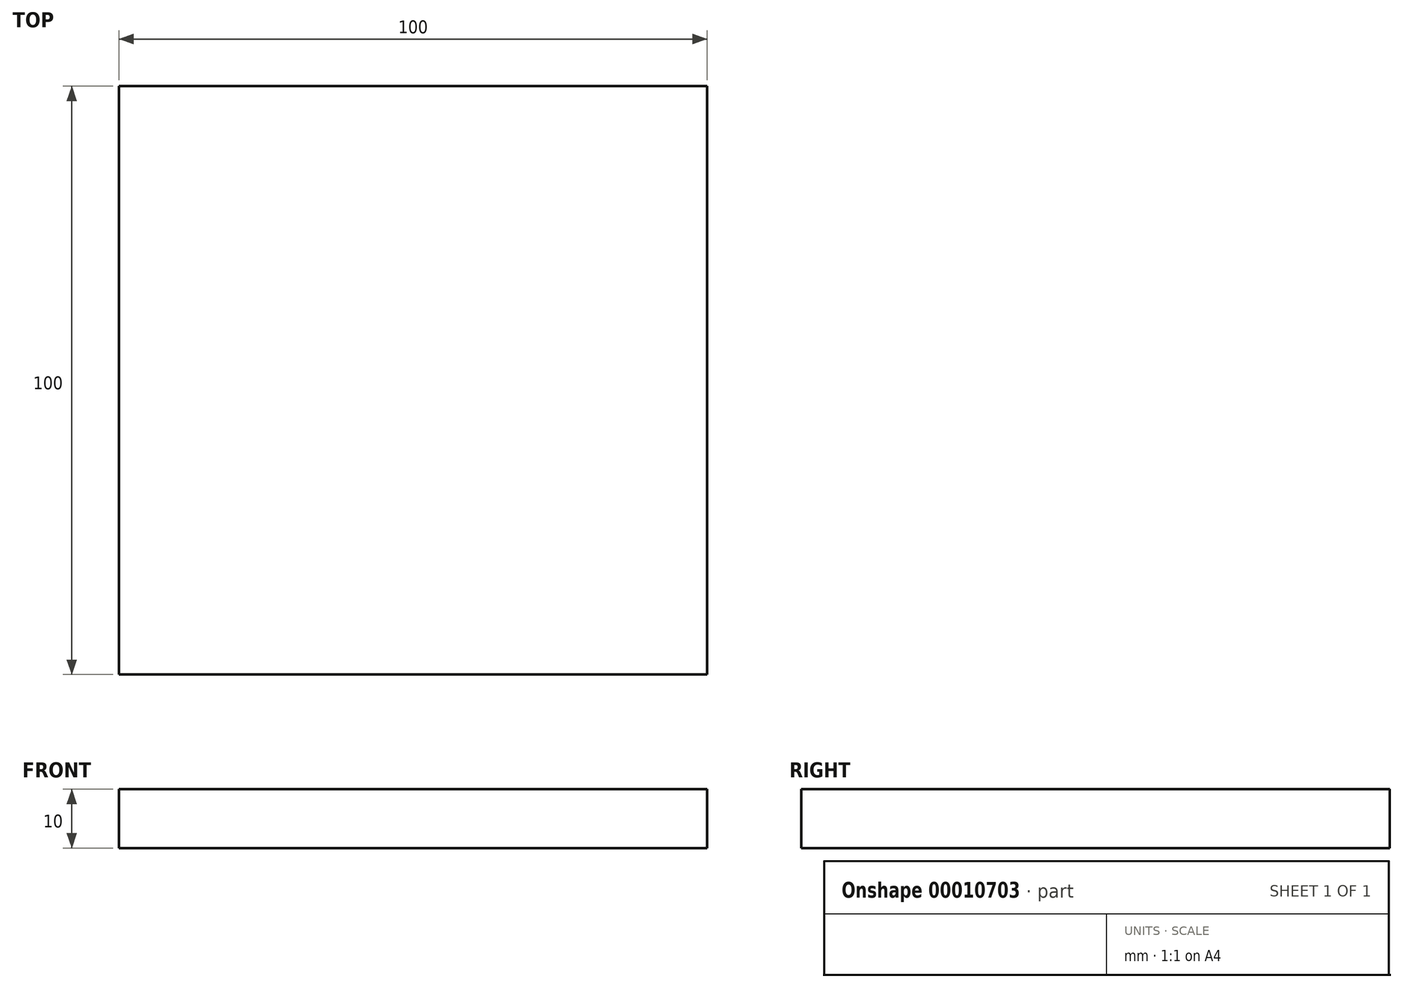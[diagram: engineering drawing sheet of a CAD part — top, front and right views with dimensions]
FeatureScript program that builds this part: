
annotation { "Feature Type Name" : "Feature", "Feature Type Description" : "" }
export const myFeature = defineFeature(function(context is Context, id is Id, definition is map)
    precondition{}
    {
        {
            var Q0;
            Q0=qCreatedBy(makeId("Top.planeOp"),FACE);
            var sketch = newSketch(context, id + "F1", { "sketchPlane" : qUnion([Q0])});
            skLineSegment(sketch, "E0.rect.bottom", {"start": v(50, 50) * mm, "end": v(-50, 50) * mm});
            skLineSegment(sketch, "E0.rect.top", {"start": v(50, -50) * mm, "end": v(-50, -50) * mm});
            skLineSegment(sketch, "E0.rect.left", {"start": v(50, 50) * mm, "end": v(50, -50) * mm});
            skLineSegment(sketch, "E0.rect.right", {"start": v(-50, 50) * mm, "end": v(-50, -50) * mm});
            skPoint(sketch, "E0.rect.middle", {"position": v(0, 0) * mm});
            skPoint(sketch, "E1.rect.bottom.start.orphan", {"position": v(50.55, 50.55) * mm});
            skPoint(sketch, "E1.rect.right.start.orphan", {"position": v(-50.55, 50.55) * mm});
            skPoint(sketch, "E1.rect.top.end.orphan", {"position": v(-50.55, -50.55) * mm});
            skPoint(sketch, "E1.rect.top.start.orphan", {"position": v(50.55, -50.55) * mm});
            skSolve(sketch);
        }
        {
            var Q0;
            Q0=makeQuery(id+"F1.imprint","IMPRINT",FACE,{"disambiguationData":[TD([[makeQuery(id+"F1.imprint","IMPRINT",EDGE,{"derivedFrom":sQuery(id+"F1.wireOp",EDGE,"E0.rect.bottom")}),-1.0]])]});
            var Q1;
            Q1=makeQuery(id+"F1.imprint","IMPRINT",FACE,{"disambiguationData":[TD([[makeQuery(id+"F1.imprint","IMPRINT",EDGE,{"derivedFrom":sQuery(id+"F1.wireOp",EDGE,"E0.rect.bottom")}),1.0]])]});
            extrude(context, id + "F0", {"entities" : qUnion([Q0, Q1]), "depth" : 10 * mm});
        }
    });
